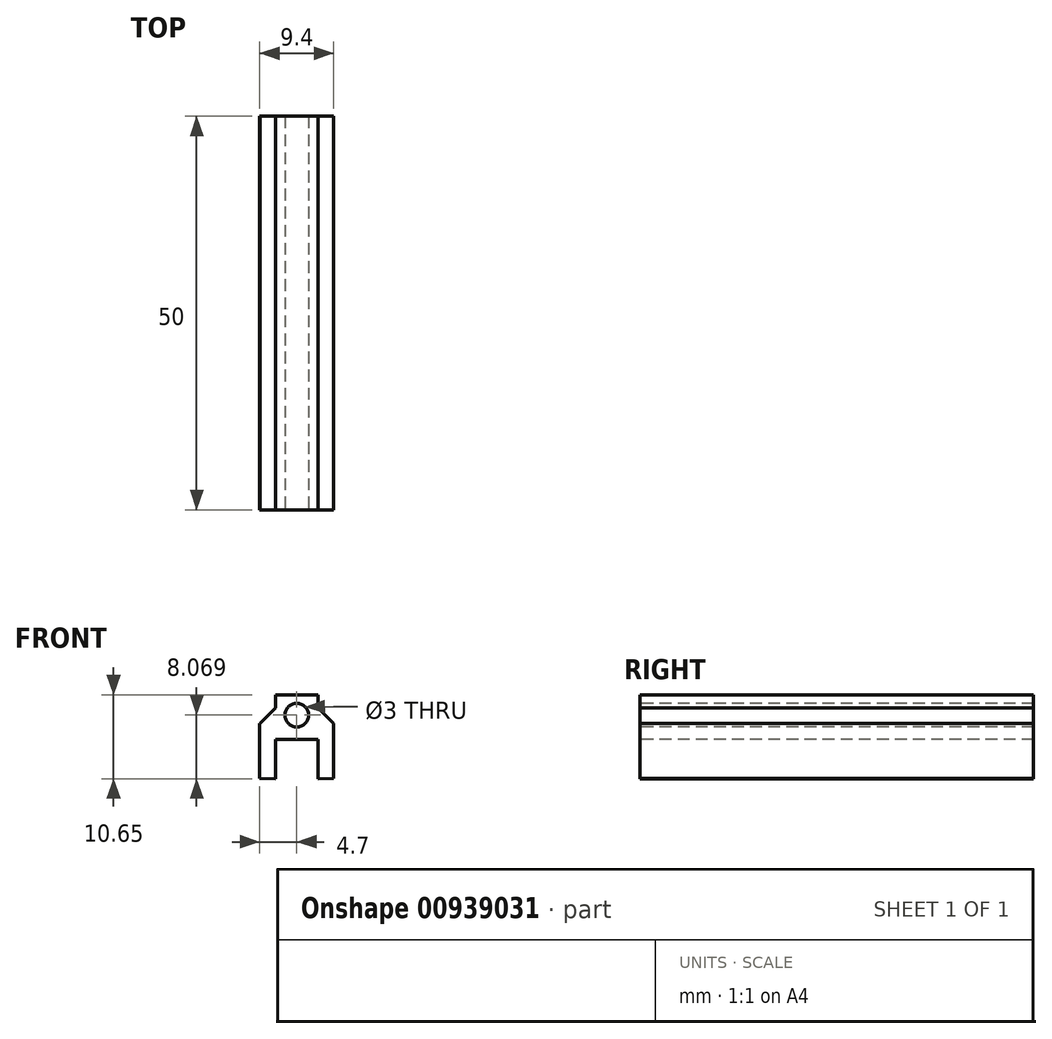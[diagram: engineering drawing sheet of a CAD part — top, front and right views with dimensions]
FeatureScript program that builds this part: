
annotation { "Feature Type Name" : "Feature", "Feature Type Description" : "" }
export const myFeature = defineFeature(function(context is Context, id is Id, definition is map)
    precondition{}
    {
        {
            var Q0;
            Q0=qCreatedBy(makeId("Front.planeOp"),FACE);
            var sketch = newSketch(context, id + "F0", { "sketchPlane" : qUnion([Q0])});
            skLineSegment(sketch, "E0", {"start": v(-2.7, 0) * mm, "end": v(2.9, 0) * mm});
            skLineSegment(sketch, "E1", {"start": v(-2.7, 0) * mm, "end": v(-2.7, -5) * mm});
            skLineSegment(sketch, "E2", {"start": v(-4.7, -4.96) * mm, "end": v(-4.7, 1.12) * mm});
            skLineSegment(sketch, "E3", {"start": v(-5.68, 2) * mm, "end": v(4.36, 2) * mm});
            skLineSegment(sketch, "E4", {"start": v(-4.7, -4.96) * mm, "end": v(-2.7, -5) * mm});
            skLineSegment(sketch, "E5", {"start": v(-4.7, 1.12) * mm, "end": v(-4.7, 2) * mm});
            skLineSegment(sketch, "E6.MirrorCS", {"start": v(2.7, 0) * mm, "end": v(2.7, -5) * mm});
            skLineSegment(sketch, "E7.MirrorCS", {"start": v(4.7, -4.96) * mm, "end": v(2.7, -5) * mm});
            skLineSegment(sketch, "E8.MirrorCS", {"start": v(4.7, -4.96) * mm, "end": v(4.7, 1.12) * mm});
            skLineSegment(sketch, "E9.MirrorCS", {"start": v(4.7, 1.12) * mm, "end": v(4.7, 2) * mm});
            skLineSegment(sketch, "E10", {"start": v(4.7, 2) * mm, "end": v(4.36, 2) * mm});
            skLineSegment(sketch, "E11", {"start": v(-2.69, 2) * mm, "end": v(-2.69, 5.65) * mm});
            skLineSegment(sketch, "E12.MirrorCS", {"start": v(2.69, 2) * mm, "end": v(2.69, 5.65) * mm});
            skLineSegment(sketch, "E13", {"start": v(-2.69, 5.65) * mm, "end": v(2.69, 5.65) * mm});
            skPoint(sketch, "E14", {"position": v(0, 3.75) * mm});
            skSolve(sketch);
        }
        {
            var Q0;
            {var subQ6=sQuery(id+"F0.wireOp",EDGE,"E1");Q0=makeQuery(id+"F0.imprint","IMPRINT",FACE,{"disambiguationData":[TD([[makeQuery(id+"F0.imprint","IMPRINT",EDGE,{"derivedFrom":subQ6}),-1.0]])]});}
            var Q1;
            {var subQ0=sQuery(id+"F0.wireOp",EDGE,"E11");Q1=makeQuery(id+"F0.imprint","IMPRINT",FACE,{"disambiguationData":[TD([[makeQuery(id+"F0.imprint","IMPRINT",EDGE,{"derivedFrom":subQ0}),-1.0]])]});}
            extrude(context, id + "F1", {"entities" : qUnion([Q0, Q1]), "oppositeDirection" : true, "depth" : 50 * mm, "offsetDistance" : 25 * mm});
        }
        {
            var Q0;
            Q0=qCreatedBy(makeId("Front.planeOp"),FACE);
            var sketch = newSketch(context, id + "F2", { "sketchPlane" : qUnion([Q0])});
            skPoint(sketch, "E15", {"position": v(0, 3.07) * mm});
            skSolve(sketch);
        }
        {
            var Q0;
            Q0=sQuery(id+"F2.wireOp",VERTEX,"E15");
            var Q1;
            Q1=makeQuery(id+"F1.opExtrude","SWEPT_BODY",BODY,{"disambiguationData":[OSD([sQuery(id+"F0.wireOp",EDGE,"E0"),sQuery(id+"F0.wireOp",EDGE,"E1"),sQuery(id+"F0.wireOp",EDGE,"E2"),sQuery(id+"F0.wireOp",EDGE,"E3"),sQuery(id+"F0.wireOp",EDGE,"E4"),sQuery(id+"F0.wireOp",EDGE,"E5"),sQuery(id+"F0.wireOp",EDGE,"E6.MirrorCS"),sQuery(id+"F0.wireOp",EDGE,"E7.MirrorCS"),sQuery(id+"F0.wireOp",EDGE,"E8.MirrorCS"),sQuery(id+"F0.wireOp",EDGE,"E9.MirrorCS"),sQuery(id+"F0.wireOp",EDGE,"E10"),sQuery(id+"F0.wireOp",EDGE,"E11"),sQuery(id+"F0.wireOp",EDGE,"E12.MirrorCS"),sQuery(id+"F0.wireOp",EDGE,"E13")])]});
            hole(context, id + "F3", {"style" : HoleStyle.SIMPLE, "endStyle" : HoleEndStyle.THROUGH, "holeDiameter" : 3 * mm, "majorDiameter" : 5 * mm, "isTappedThrough" : true, "tappedDepth" : 12.7 * mm, "tapClearance" : 3, "startFromSketch" : true, "locations" : qUnion([Q0]), "scope" : qUnion([Q1])});
        }
        {
            var Q0;
            Q0=makeQuery(id+"F1.opExtrude","SWEPT_EDGE",EDGE,{"disambiguationData":[OSD([sQuery(id+"F0.wireOp",EDGE,"E3"),sQuery(id+"F0.wireOp",EDGE,"E12.MirrorCS")])]});
            var Q1;
            Q1=makeQuery(id+"F1.opExtrude","SWEPT_EDGE",EDGE,{"disambiguationData":[OSD([sQuery(id+"F0.wireOp",EDGE,"E3"),sQuery(id+"F0.wireOp",EDGE,"E11")])]});
            chamfer(context, id + "F4", {"entities" : qUnion([Q0, Q1]), "width" : 2 * mm, "tangentPropagation" : true});
        }
    });
